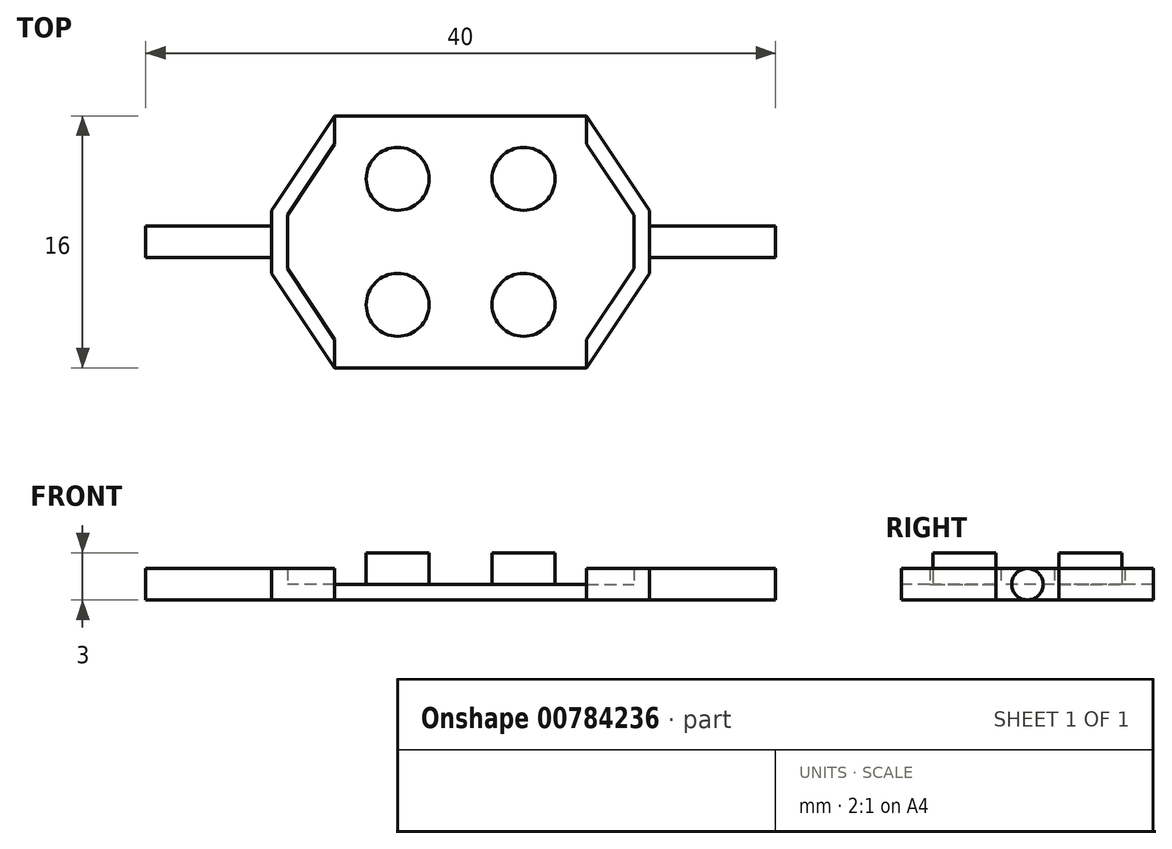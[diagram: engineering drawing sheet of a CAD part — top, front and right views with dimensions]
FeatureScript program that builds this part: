
annotation { "Feature Type Name" : "Feature", "Feature Type Description" : "" }
export const myFeature = defineFeature(function(context is Context, id is Id, definition is map)
    precondition{}
    {
        {
            var Q0;
            Q0=qCreatedBy(makeId("Top.planeOp"),FACE);
            var sketch = newSketch(context, id + "F0", { "sketchPlane" : qUnion([Q0])});
            skLineSegment(sketch, "E0", {"start": v(0, 0) * mm, "end": v(-12, 0) * mm});
            skLineSegment(sketch, "E1", {"start": v(-12, 0) * mm, "end": v(-12, 2) * mm});
            skLineSegment(sketch, "E2", {"start": v(0, 0) * mm, "end": v(0, 8) * mm});
            skLineSegment(sketch, "E3", {"start": v(0, 8) * mm, "end": v(-8, 8) * mm});
            skLineSegment(sketch, "E4", {"start": v(-8, 8) * mm, "end": v(-12, 2) * mm});
            skLineSegment(sketch, "E5.MirrorCS", {"start": v(-12, 0) * mm, "end": v(-12, -2) * mm});
            skLineSegment(sketch, "E6.MirrorCS", {"start": v(-8, -8) * mm, "end": v(-12, -2) * mm});
            skLineSegment(sketch, "E7.MirrorCS", {"start": v(0, -8) * mm, "end": v(-8, -8) * mm});
            skLineSegment(sketch, "E8.MirrorCS", {"start": v(0, 0) * mm, "end": v(0, -8) * mm});
            skSolve(sketch);
        }
        {
            var Q0;
            Q0=makeQuery(id+"F0.imprint","IMPRINT",FACE,{"disambiguationData":[TD([[makeQuery(id+"F0.imprint","IMPRINT",EDGE,{"derivedFrom":sQuery(id+"F0.wireOp",EDGE,"E0")}),1.0]])]});
            var Q1;
            Q1=makeQuery(id+"F0.imprint","IMPRINT",FACE,{"disambiguationData":[TD([[makeQuery(id+"F0.imprint","IMPRINT",EDGE,{"derivedFrom":sQuery(id+"F0.wireOp",EDGE,"E0")}),-1.0]])]});
            extrude(context, id + "F1", {"entities" : qUnion([Q0, Q1]), "depth" : 1 * mm});
        }
        {
            var Q0;
            Q0=makeQuery(id+"F1.opExtrude","CAP_FACE",FACE,{"disambiguationData":[OSD([sQuery(id+"F0.wireOp",EDGE,"E1"),sQuery(id+"F0.wireOp",EDGE,"E2"),sQuery(id+"F0.wireOp",EDGE,"E3"),sQuery(id+"F0.wireOp",EDGE,"E4"),sQuery(id+"F0.wireOp",EDGE,"E5.MirrorCS"),sQuery(id+"F0.wireOp",EDGE,"E6.MirrorCS"),sQuery(id+"F0.wireOp",EDGE,"E7.MirrorCS"),sQuery(id+"F0.wireOp",EDGE,"E8.MirrorCS")])],"isStart":false});
            var sketch = newSketch(context, id + "F2", { "sketchPlane" : qUnion([Q0])});
            skCircle(sketch, "E9", {"center": v(-4, 4) * mm, "radius": 2 * mm});
            skCircle(sketch, "E10.MirrorC", {"center": v(-4, -4) * mm, "radius": 2 * mm});
            skSolve(sketch);
        }
        {
            var Q0;
            Q0=qSketchRegion(id+"F2",true);
            extrude(context, id + "F3", {"entities" : qUnion([Q0]), "operationType" : NewBodyOperationType.ADD, "depth" : 2 * mm});
        }
        {
            var Q0;
            Q0=makeQuery(id+"F1.opExtrude","CAP_FACE",FACE,{"disambiguationData":[OSD([sQuery(id+"F0.wireOp",EDGE,"E1"),sQuery(id+"F0.wireOp",EDGE,"E2"),sQuery(id+"F0.wireOp",EDGE,"E3"),sQuery(id+"F0.wireOp",EDGE,"E4"),sQuery(id+"F0.wireOp",EDGE,"E5.MirrorCS"),sQuery(id+"F0.wireOp",EDGE,"E6.MirrorCS"),sQuery(id+"F0.wireOp",EDGE,"E7.MirrorCS"),sQuery(id+"F0.wireOp",EDGE,"E8.MirrorCS")])],"isStart":false});
            var sketch = newSketch(context, id + "F4", { "sketchPlane" : qUnion([Q0])});
            skLineSegment(sketch, "E11", {"start": v(-8, 8) * mm, "end": v(-8, 6.2) * mm});
            skLineSegment(sketch, "E12.0", {"start": v(-8, -6.2) * mm, "end": v(-11, -1.7) * mm});
            skLineSegment(sketch, "E12.1", {"start": v(-11, 1.7) * mm, "end": v(-11, -1.7) * mm});
            skLineSegment(sketch, "E12.2", {"start": v(-8, 6.2) * mm, "end": v(-11, 1.7) * mm});
            skLineSegment(sketch, "E13.trimOffspring", {"start": v(-8, -6.2) * mm, "end": v(-8, -8) * mm});
            skLineSegment(sketch, "E14", {"start": v(-8, -8) * mm, "end": v(-12, -2) * mm});
            skLineSegment(sketch, "E15", {"start": v(-12, -2) * mm, "end": v(-12, 2) * mm});
            skLineSegment(sketch, "E16", {"start": v(-12, 2) * mm, "end": v(-8, 8) * mm});
            skSolve(sketch);
        }
        {
            var Q0;
            Q0=qSketchRegion(id+"F4",true);
            extrude(context, id + "F5", {"entities" : qUnion([Q0]), "depth" : 1 * mm});
        }
        {
            var Q0;
            Q0=makeQuery(id+"F1.opExtrude","SWEPT_BODY",BODY,{"disambiguationData":[OSD([sQuery(id+"F0.wireOp",EDGE,"E1"),sQuery(id+"F0.wireOp",EDGE,"E2"),sQuery(id+"F0.wireOp",EDGE,"E3"),sQuery(id+"F0.wireOp",EDGE,"E4"),sQuery(id+"F0.wireOp",EDGE,"E5.MirrorCS"),sQuery(id+"F0.wireOp",EDGE,"E6.MirrorCS"),sQuery(id+"F0.wireOp",EDGE,"E7.MirrorCS"),sQuery(id+"F0.wireOp",EDGE,"E8.MirrorCS")])]});
            var Q1;
            Q1=makeQuery(id+"F5.opExtrude","SWEPT_BODY",BODY,{"disambiguationData":[OSD([sQuery(id+"F4.wireOp",EDGE,"E11"),sQuery(id+"F4.wireOp",EDGE,"E12.0"),sQuery(id+"F4.wireOp",EDGE,"E12.1"),sQuery(id+"F4.wireOp",EDGE,"E12.2"),sQuery(id+"F4.wireOp",EDGE,"E13.trimOffspring"),sQuery(id+"F4.wireOp",EDGE,"E14"),sQuery(id+"F4.wireOp",EDGE,"E15"),sQuery(id+"F4.wireOp",EDGE,"E16")])]});
            booleanBodies(context, id + "F6", {"operationType" : BooleanOperationType.UNION, "tools" : qUnion([Q0, Q1])});
        }
        {
            var Q0;
            Q0=makeQuery(id+"F6.opBoolean","MERGE",FACE,{"derivedFrom":[makeQuery(id+"F1.opExtrude","SWEPT_FACE",FACE,{"disambiguationData":[OSD([sQuery(id+"F0.wireOp",EDGE,"E1"),sQuery(id+"F0.wireOp",EDGE,"E5.MirrorCS")])]}),makeQuery(id+"F5.opExtrude","SWEPT_FACE",FACE,{"disambiguationData":[OSD([sQuery(id+"F4.wireOp",EDGE,"E15")])]})]});
            var sketch = newSketch(context, id + "F7", { "sketchPlane" : qUnion([Q0])});
            skCircle(sketch, "E17", {"center": v(0, 1) * mm, "radius": 1 * mm});
            skSolve(sketch);
        }
        {
            var Q0;
            {var subQ0=sQuery(id+"F7.wireOp",EDGE,"E17");var subQ2=makeQuery(id+"F7.imprint","INTERSECT",VERTEX,{"derivedFrom":[makeQuery(id+"F5.opExtrude","CAP_EDGE",EDGE,{"disambiguationData":[OSD([sQuery(id+"F4.wireOp",EDGE,"E15")])],"isStart":false}),subQ0]});Q0=makeQuery(id+"F7.imprint","IMPRINT",FACE,{"disambiguationData":[TD([[makeQuery(id+"F7.imprint","IMPRINT",EDGE,{"disambiguationData":[TD([[subQ2,-1.0]])],"derivedFrom":subQ0}),1.0]])]});}
            extrude(context, id + "F8", {"entities" : qUnion([Q0]), "operationType" : NewBodyOperationType.ADD, "depth" : 8 * mm});
        }
        {
            var Q0;
            Q0=makeQuery(id+"F1.opExtrude","SWEPT_BODY",BODY,{"disambiguationData":[OSD([sQuery(id+"F0.wireOp",EDGE,"E1"),sQuery(id+"F0.wireOp",EDGE,"E2"),sQuery(id+"F0.wireOp",EDGE,"E3"),sQuery(id+"F0.wireOp",EDGE,"E4"),sQuery(id+"F0.wireOp",EDGE,"E5.MirrorCS"),sQuery(id+"F0.wireOp",EDGE,"E6.MirrorCS"),sQuery(id+"F0.wireOp",EDGE,"E7.MirrorCS"),sQuery(id+"F0.wireOp",EDGE,"E8.MirrorCS")])]});
            var Q1;
            Q1=makeQuery(id+"F1.opExtrude","SWEPT_FACE",FACE,{"disambiguationData":[OSD([sQuery(id+"F0.wireOp",EDGE,"E2"),sQuery(id+"F0.wireOp",EDGE,"E8.MirrorCS")])]});
            mirror(context, id + "F9", {"operationType" : NewBodyOperationType.ADD, "entities" : qUnion([Q0]), "mirrorPlane" : qUnion([Q1])});
        }
    });
